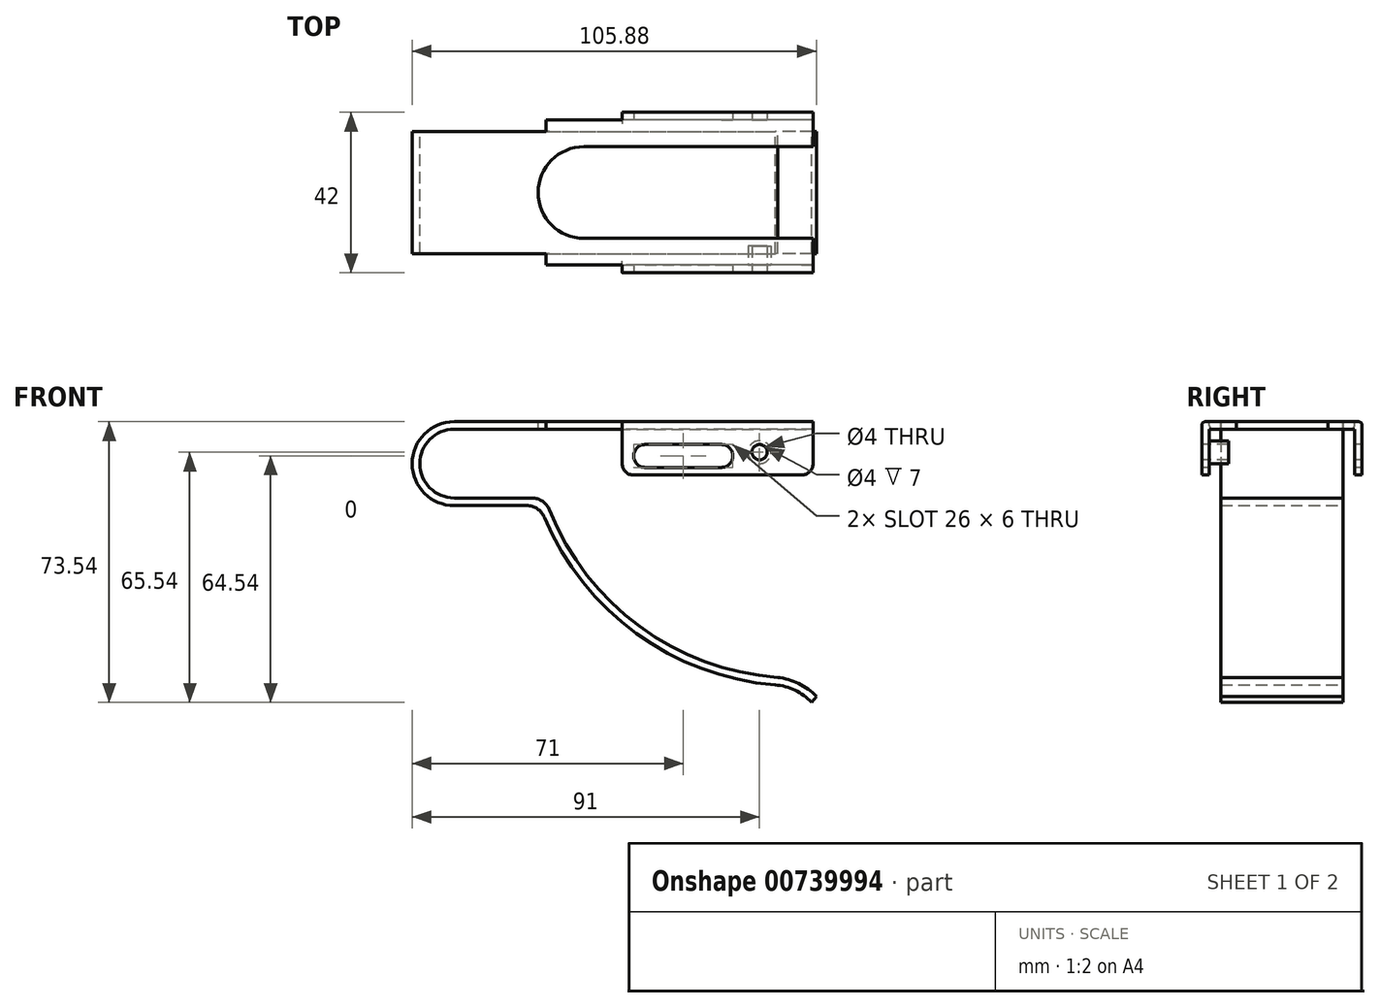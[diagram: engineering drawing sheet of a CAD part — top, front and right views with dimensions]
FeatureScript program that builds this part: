
annotation { "Feature Type Name" : "Feature", "Feature Type Description" : "" }
export const myFeature = defineFeature(function(context is Context, id is Id, definition is map)
    precondition{}
    {
        {
            var Q0;
            Q0=qCreatedBy(makeId("Front.planeOp"),FACE);
            var sketch = newSketch(context, id + "F0", { "sketchPlane" : qUnion([Q0])});
            skArc(sketch, "E0", {"start": v(0, 9) * mm, "mid": v(-9, 0) * mm, "end": v(0, -9) * mm});
            skLineSegment(sketch, "E1", {"start": v(0, 9) * mm, "end": v(94, 9) * mm});
            skLineSegment(sketch, "E2", {"start": v(0, -9) * mm, "end": v(20.34, -9) * mm});
            skArc(sketch, "E3", {"start": v(24.99, -12.15) * mm, "mid": v(48.57, -42.62) * mm, "end": v(84.7, -56) * mm});
            skArc(sketch, "E4", {"start": v(94.88, -61) * mm, "mid": v(90.25, -57.57) * mm, "end": v(84.7, -56) * mm});
            skPoint(sketch, "E5.visualSharp", {"position": v(23.82, -9) * mm});
            skArc(sketch, "E5.filletArc", {"start": v(24.99, -12.15) * mm, "mid": v(23.15, -9.86) * mm, "end": v(20.34, -9) * mm});
            skArc(sketch, "E6.0", {"start": v(93.59, -62.54) * mm, "mid": v(89.28, -59.32) * mm, "end": v(84.08, -57.96) * mm});
            skLineSegment(sketch, "E6.1", {"start": v(0, 11) * mm, "end": v(94, 11) * mm});
            skArc(sketch, "E6.2", {"start": v(0, 11) * mm, "mid": v(-11, 0) * mm, "end": v(0, -11) * mm});
            skLineSegment(sketch, "E6.3", {"start": v(0, -11) * mm, "end": v(19, -11) * mm});
            skArc(sketch, "E6.4", {"start": v(23.61, -14.06) * mm, "mid": v(47.7, -44.47) * mm, "end": v(84.08, -57.96) * mm});
            skLineSegment(sketch, "E7", {"start": v(94, 9) * mm, "end": v(94, 11) * mm});
            skLineSegment(sketch, "E8", {"start": v(93.59, -62.54) * mm, "end": v(94.88, -61) * mm});
            skPoint(sketch, "E9.visualSharp", {"position": v(22.4, -11) * mm});
            skArc(sketch, "E9.filletArc", {"start": v(23.61, -14.06) * mm, "mid": v(21.77, -11.84) * mm, "end": v(19, -11) * mm});
            skLineSegment(sketch, "E10", {"start": v(94.88, -61) * mm, "end": v(137.33, -61) * mm});
            skSolve(sketch);
        }
        {
            var Q0;
            Q0 = qSketchRegion(id + "F0", true);
            extrude(context, id + "F1", {"entities" : qUnion([Q0]), "depth" : 16 * mm, "offsetDistance" : 25 * mm});
        }
        {
            var Q0;
            Q0=makeQuery(id+"F1.opExtrude","SWEPT_FACE",FACE,{"disambiguationData":[OSD([sQuery(id+"F0.wireOp",EDGE,"E6.1")])]});
            var sketch = newSketch(context, id + "F2", { "sketchPlane" : qUnion([Q0])});
            skLineSegment(sketch, "E11.bottom", {"start": v(94, -16) * mm, "end": v(24, -16) * mm});
            skLineSegment(sketch, "E11.top", {"start": v(94, -19) * mm, "end": v(24, -19) * mm});
            skLineSegment(sketch, "E11.left", {"start": v(94, -16) * mm, "end": v(94, -19) * mm});
            skLineSegment(sketch, "E11.right", {"start": v(24, -16) * mm, "end": v(24, -19) * mm});
            skSolve(sketch);
        }
        {
            var Q0;
            Q0 = qSketchRegion(id + "F2", true);
            extrude(context, id + "F3", {"entities" : qUnion([Q0]), "operationType" : NewBodyOperationType.ADD, "oppositeDirection" : true, "depth" : 2 * mm, "offsetDistance" : 25 * mm});
        }
        {
            var Q0;
            Q0=makeQuery(id+"F3.opExtrude","SWEPT_FACE",FACE,{"disambiguationData":[OSD([sQuery(id+"F2.wireOp",EDGE,"E11.top")])]});
            var sketch = newSketch(context, id + "F4", { "sketchPlane" : qUnion([Q0])});
            skLineSegment(sketch, "E12.bottom", {"start": v(94, 11) * mm, "end": v(44, 11) * mm});
            skLineSegment(sketch, "E12.top", {"start": v(94, -3) * mm, "end": v(44, -3) * mm});
            skLineSegment(sketch, "E12.left", {"start": v(94, 11) * mm, "end": v(94, -3) * mm});
            skLineSegment(sketch, "E12.right", {"start": v(44, 11) * mm, "end": v(44, -3) * mm});
            skSolve(sketch);
        }
        {
            var Q0;
            Q0 = qSketchRegion(id + "F4", true);
            extrude(context, id + "F5", {"entities" : qUnion([Q0]), "operationType" : NewBodyOperationType.ADD, "depth" : 2 * mm, "offsetDistance" : 25 * mm});
        }
        {
            var Q0;
            Q0=makeQuery(id+"F5.opExtrude","CAP_EDGE",EDGE,{"disambiguationData":[OSD([sQuery(id+"F4.wireOp",EDGE,"E12.bottom")])],"isStart":false});
            var Q1;
            {var subQ0=sQuery(id+"F2.wireOp",EDGE,"E11.top");Q1=makeQuery(id+"F5.boolean.opBoolean","SPLIT",EDGE,{"disambiguationData":[topologyDisambiguationEdgeConnected([makeQuery(id+"F5.opExtrude","CAP_FACE",FACE,{"disambiguationData":[OSD([sQuery(id+"F4.wireOp",EDGE,"E12.bottom"),sQuery(id+"F4.wireOp",EDGE,"E12.top"),sQuery(id+"F4.wireOp",EDGE,"E12.left"),sQuery(id+"F4.wireOp",EDGE,"E12.right")])],"isStart":true})])],"derivedFrom":makeQuery(id+"F3.opExtrude","CAP_EDGE",EDGE,{"disambiguationData":[OSD([subQ0])],"isStart":false})});}
            fillet(context, id + "F6", {"entities" : qUnion([Q0, Q1]), "radius" : 1 * mm, "tangentPropagation" : true, "allowEdgeOverflow" : false});
        }
        {
            var Q0;
            Q0=makeQuery(id+"F1.opExtrude","SWEPT_BODY",BODY,{"disambiguationData":[OSD([sQuery(id+"F0.wireOp",EDGE,"E0"),sQuery(id+"F0.wireOp",EDGE,"E1"),sQuery(id+"F0.wireOp",EDGE,"E2"),sQuery(id+"F0.wireOp",EDGE,"E3"),sQuery(id+"F0.wireOp",EDGE,"E4"),sQuery(id+"F0.wireOp",EDGE,"E5.filletArc"),sQuery(id+"F0.wireOp",EDGE,"E6.0"),sQuery(id+"F0.wireOp",EDGE,"E6.1"),sQuery(id+"F0.wireOp",EDGE,"E6.2"),sQuery(id+"F0.wireOp",EDGE,"E6.3"),sQuery(id+"F0.wireOp",EDGE,"E6.4"),sQuery(id+"F0.wireOp",EDGE,"E7"),sQuery(id+"F0.wireOp",EDGE,"E8"),sQuery(id+"F0.wireOp",EDGE,"E9.filletArc")])]});
            var Q1;
            Q1=qCreatedBy(makeId("Front.planeOp"),FACE);
            mirror(context, id + "F7", {"operationType" : NewBodyOperationType.ADD, "entities" : qUnion([Q0]), "mirrorPlane" : qUnion([Q1])});
        }
        {
            var Q0;
            {var subQ0=makeQuery(id+"F5.boolean.opBoolean","MERGE",FACE,{"derivedFrom":[makeQuery(id+"F3.boolean.opBoolean","MERGE",FACE,{"derivedFrom":[makeQuery(id+"F1.opExtrude","SWEPT_FACE",FACE,{"disambiguationData":[OSD([sQuery(id+"F0.wireOp",EDGE,"E6.1")])]}),makeQuery(id+"F3.opExtrude","CAP_FACE",FACE,{"disambiguationData":[OSD([sQuery(id+"F2.wireOp",EDGE,"E11.bottom"),sQuery(id+"F2.wireOp",EDGE,"E11.top"),sQuery(id+"F2.wireOp",EDGE,"E11.left"),sQuery(id+"F2.wireOp",EDGE,"E11.right")])],"isStart":true})]}),makeQuery(id+"F5.opExtrude","SWEPT_FACE",FACE,{"disambiguationData":[OSD([sQuery(id+"F4.wireOp",EDGE,"E12.bottom")])]})]});Q0=makeQuery(id+"F7.boolean.opBoolean","MERGE",FACE,{"derivedFrom":[subQ0,makeQuery(id+"F7.opPattern","COPY",FACE,{"derivedFrom":subQ0,"instanceName":"1"})]});}
            var sketch = newSketch(context, id + "F8", { "sketchPlane" : qUnion([Q0])});
            skArc(sketch, "E13", {"start": v(34, 12) * mm, "mid": v(22, 0) * mm, "end": v(34, -12) * mm});
            skLineSegment(sketch, "E14", {"start": v(34, 12) * mm, "end": v(94, 12) * mm});
            skLineSegment(sketch, "E15", {"start": v(34, -12) * mm, "end": v(94, -12) * mm});
            skLineSegment(sketch, "E16", {"start": v(94, 12) * mm, "end": v(94, -12) * mm});
            skSolve(sketch);
        }
        {
            var Q0;
            Q0 = qSketchRegion(id + "F8", true);
            extrude(context, id + "F9", {"entities" : qUnion([Q0]), "operationType" : NewBodyOperationType.REMOVE, "oppositeDirection" : true, "depth" : 2 * mm, "offsetDistance" : 25 * mm});
        }
        {
            var Q0;
            Q0=makeQuery(id+"F5.opExtrude","CAP_FACE",FACE,{"disambiguationData":[OSD([sQuery(id+"F4.wireOp",EDGE,"E12.bottom"),sQuery(id+"F4.wireOp",EDGE,"E12.top"),sQuery(id+"F4.wireOp",EDGE,"E12.left"),sQuery(id+"F4.wireOp",EDGE,"E12.right")])],"isStart":false});
            var sketch = newSketch(context, id + "F10", { "sketchPlane" : qUnion([Q0])});
            skLineSegment(sketch, "E17", {"start": v(50, 2) * mm, "end": v(70, 2) * mm});
            skArc(sketch, "E18.0.startCap", {"start": v(50, -1) * mm, "mid": v(47, 2) * mm, "end": v(50, 5) * mm});
            skArc(sketch, "E18.0.endCap", {"start": v(70, 5) * mm, "mid": v(73, 2) * mm, "end": v(70, -1) * mm});
            skLineSegment(sketch, "E18.0.left", {"start": v(50, 5) * mm, "end": v(70, 5) * mm});
            skLineSegment(sketch, "E18.0.right", {"start": v(50, -1) * mm, "end": v(70, -1) * mm});
            skSolve(sketch);
        }
        {
            var Q0;
            Q0 = qSketchRegion(id + "F10", true);
            extrude(context, id + "F11", {"entities" : qUnion([Q0]), "operationType" : NewBodyOperationType.REMOVE, "endBound" : BoundingType.THROUGH_ALL, "oppositeDirection" : true, "depth" : 25 * mm, "offsetDistance" : 25 * mm});
        }
        {
            var Q0;
            Q0=makeQuery(id+"F5.opExtrude","CAP_FACE",FACE,{"disambiguationData":[OSD([sQuery(id+"F4.wireOp",EDGE,"E12.bottom"),sQuery(id+"F4.wireOp",EDGE,"E12.top"),sQuery(id+"F4.wireOp",EDGE,"E12.left"),sQuery(id+"F4.wireOp",EDGE,"E12.right")])],"isStart":false});
            var sketch = newSketch(context, id + "F12", { "sketchPlane" : qUnion([Q0])});
            skPoint(sketch, "E19", {"position": v(80, 3) * mm});
            skSolve(sketch);
        }
        {
            var Q0;
            Q0=sQuery(id+"F12.wireOp",VERTEX,"E19");
            var Q1;
            Q1=makeQuery(id+"F1.opExtrude","SWEPT_BODY",BODY,{"disambiguationData":[OSD([sQuery(id+"F0.wireOp",EDGE,"E0"),sQuery(id+"F0.wireOp",EDGE,"E1"),sQuery(id+"F0.wireOp",EDGE,"E2"),sQuery(id+"F0.wireOp",EDGE,"E3"),sQuery(id+"F0.wireOp",EDGE,"E4"),sQuery(id+"F0.wireOp",EDGE,"E5.filletArc"),sQuery(id+"F0.wireOp",EDGE,"E6.0"),sQuery(id+"F0.wireOp",EDGE,"E6.1"),sQuery(id+"F0.wireOp",EDGE,"E6.2"),sQuery(id+"F0.wireOp",EDGE,"E6.3"),sQuery(id+"F0.wireOp",EDGE,"E6.4"),sQuery(id+"F0.wireOp",EDGE,"E7"),sQuery(id+"F0.wireOp",EDGE,"E8"),sQuery(id+"F0.wireOp",EDGE,"E9.filletArc")])]});
            hole(context, id + "F13", {"style" : HoleStyle.SIMPLE, "endStyle" : HoleEndStyle.THROUGH, "holeDiameter" : 4 * mm, "majorDiameter" : 5 * mm, "isTappedThrough" : true, "tappedDepth" : 12 * mm, "tapClearance" : 3, "locations" : qUnion([Q0]), "scope" : qUnion([Q1])});
        }
        {
            var Q0;
            Q0=makeQuery(id+"F5.opExtrude","CAP_FACE",FACE,{"disambiguationData":[OSD([sQuery(id+"F4.wireOp",EDGE,"E12.bottom"),sQuery(id+"F4.wireOp",EDGE,"E12.top"),sQuery(id+"F4.wireOp",EDGE,"E12.left"),sQuery(id+"F4.wireOp",EDGE,"E12.right")])],"isStart":true});
            var sketch = newSketch(context, id + "F14", { "sketchPlane" : qUnion([Q0])});
            skCircle(sketch, "E20.0", {"center": v(-80, 3) * mm, "radius": 2 * mm});
            skCircle(sketch, "E21.0", {"center": v(-80, 3) * mm, "radius": 3 * mm});
            skSolve(sketch);
        }
        {
            var Q0;
            Q0 = qSketchRegion(id + "F14", true);
            extrude(context, id + "F15", {"entities" : qUnion([Q0]), "operationType" : NewBodyOperationType.ADD, "depth" : 5 * mm, "offsetDistance" : 25 * mm});
        }
        {
            var Q0;
            Q0=makeQuery(id+"F7.opPattern","COPY",EDGE,{"derivedFrom":makeQuery(id+"F5.opExtrude","SWEPT_EDGE",EDGE,{"disambiguationData":[OSD([sQuery(id+"F4.wireOp",EDGE,"E12.top"),sQuery(id+"F4.wireOp",EDGE,"E12.left")])]}),"instanceName":"1"});
            var Q1;
            Q1=makeQuery(id+"F7.opPattern","COPY",EDGE,{"derivedFrom":makeQuery(id+"F5.opExtrude","SWEPT_EDGE",EDGE,{"disambiguationData":[OSD([sQuery(id+"F4.wireOp",EDGE,"E12.top"),sQuery(id+"F4.wireOp",EDGE,"E12.right")])]}),"instanceName":"1"});
            var Q2;
            Q2=makeQuery(id+"F5.opExtrude","SWEPT_EDGE",EDGE,{"disambiguationData":[OSD([sQuery(id+"F4.wireOp",EDGE,"E12.top"),sQuery(id+"F4.wireOp",EDGE,"E12.right")])]});
            var Q3;
            Q3=makeQuery(id+"F5.opExtrude","SWEPT_EDGE",EDGE,{"disambiguationData":[OSD([sQuery(id+"F4.wireOp",EDGE,"E12.top"),sQuery(id+"F4.wireOp",EDGE,"E12.left")])]});
            fillet(context, id + "F16", {"entities" : qUnion([Q0, Q1, Q2, Q3]), "radius" : 3 * mm, "tangentPropagation" : true, "allowEdgeOverflow" : false});
        }
    });
